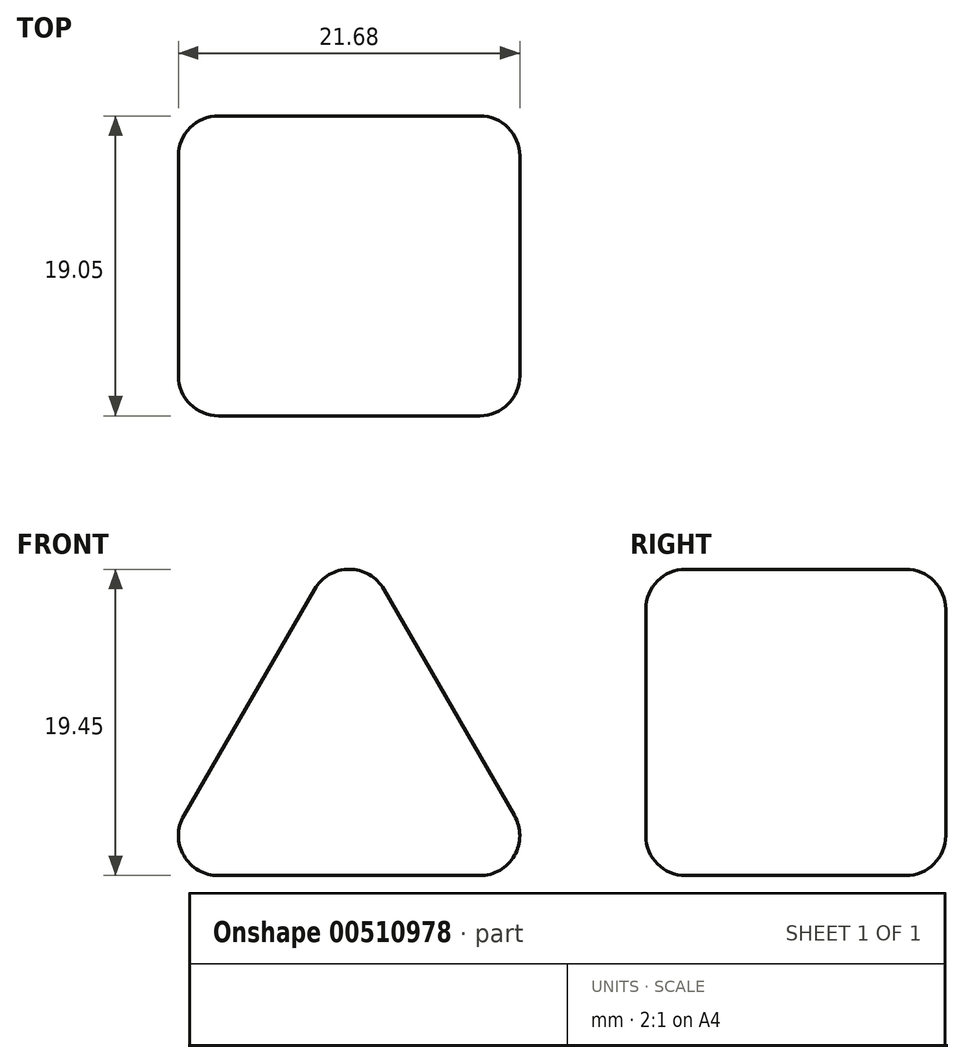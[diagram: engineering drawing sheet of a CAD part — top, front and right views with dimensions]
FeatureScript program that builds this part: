
annotation { "Feature Type Name" : "Feature", "Feature Type Description" : "" }
export const myFeature = defineFeature(function(context is Context, id is Id, definition is map)
    precondition{}
    {
        {
            var Q0;
            Q0=qCreatedBy(makeId("Front.planeOp"),FACE);
            var sketch = newSketch(context, id + "F0", { "sketchPlane" : qUnion([Q0])});
            skCircle(sketch, "E0.cCircle", {"center": v(0, 22.15) * mm, "radius": 7.33 * mm, "construction": true});
            skLineSegment(sketch, "E0.0", {"start": v(12.7, 14.82) * mm, "end": v(-12.7, 14.82) * mm});
            skLineSegment(sketch, "E0.1", {"start": v(-12.7, 14.82) * mm, "end": v(0, 36.81) * mm});
            skLineSegment(sketch, "E0.2", {"start": v(0, 36.81) * mm, "end": v(12.7, 14.82) * mm});
            skPoint(sketch, "E0.0.midPoint", {"position": v(0, 14.82) * mm});
            skSolve(sketch);
        }
        {
            var Q0;
            Q0 = qSketchRegion(id + "F0", true);
            extrude(context, id + "F1", {"entities" : qUnion([Q0]), "depth" : 19.05 * mm});
        }
        {
            var Q0;
            Q0=makeQuery(id+"F1.opExtrude","SWEPT_EDGE",EDGE,{"disambiguationData":[OSD([sQuery(id+"F0.wireOp",EDGE,"E0.1"),sQuery(id+"F0.wireOp",EDGE,"E0.2")])]});
            var Q1;
            Q1=makeQuery(id+"F1.opExtrude","CAP_EDGE",EDGE,{"disambiguationData":[OSD([sQuery(id+"F0.wireOp",EDGE,"E0.1")])],"isStart":false});
            var Q2;
            Q2=makeQuery(id+"F1.opExtrude","CAP_EDGE",EDGE,{"disambiguationData":[OSD([sQuery(id+"F0.wireOp",EDGE,"E0.2")])],"isStart":false});
            var Q3;
            Q3=makeQuery(id+"F1.opExtrude","CAP_EDGE",EDGE,{"disambiguationData":[OSD([sQuery(id+"F0.wireOp",EDGE,"E0.1")])],"isStart":true});
            var Q4;
            Q4=makeQuery(id+"F1.opExtrude","CAP_EDGE",EDGE,{"disambiguationData":[OSD([sQuery(id+"F0.wireOp",EDGE,"E0.2")])],"isStart":true});
            var Q5;
            Q5=makeQuery(id+"F1.opExtrude","CAP_EDGE",EDGE,{"disambiguationData":[OSD([sQuery(id+"F0.wireOp",EDGE,"E0.0")])],"isStart":true});
            var Q6;
            Q6=makeQuery(id+"F1.opExtrude","SWEPT_EDGE",EDGE,{"disambiguationData":[OSD([sQuery(id+"F0.wireOp",EDGE,"E0.0"),sQuery(id+"F0.wireOp",EDGE,"E0.1")])]});
            var Q7;
            Q7=makeQuery(id+"F1.opExtrude","CAP_EDGE",EDGE,{"disambiguationData":[OSD([sQuery(id+"F0.wireOp",EDGE,"E0.0")])],"isStart":false});
            var Q8;
            Q8=makeQuery(id+"F1.opExtrude","SWEPT_EDGE",EDGE,{"disambiguationData":[OSD([sQuery(id+"F0.wireOp",EDGE,"E0.0"),sQuery(id+"F0.wireOp",EDGE,"E0.2")])]});
            fillet(context, id + "F2", {"entities" : qUnion([Q0, Q1, Q2, Q3, Q4, Q5, Q6, Q7, Q8]), "radius" : 2.54 * mm, "tangentPropagation" : true, "allowEdgeOverflow" : false});
        }
    });
